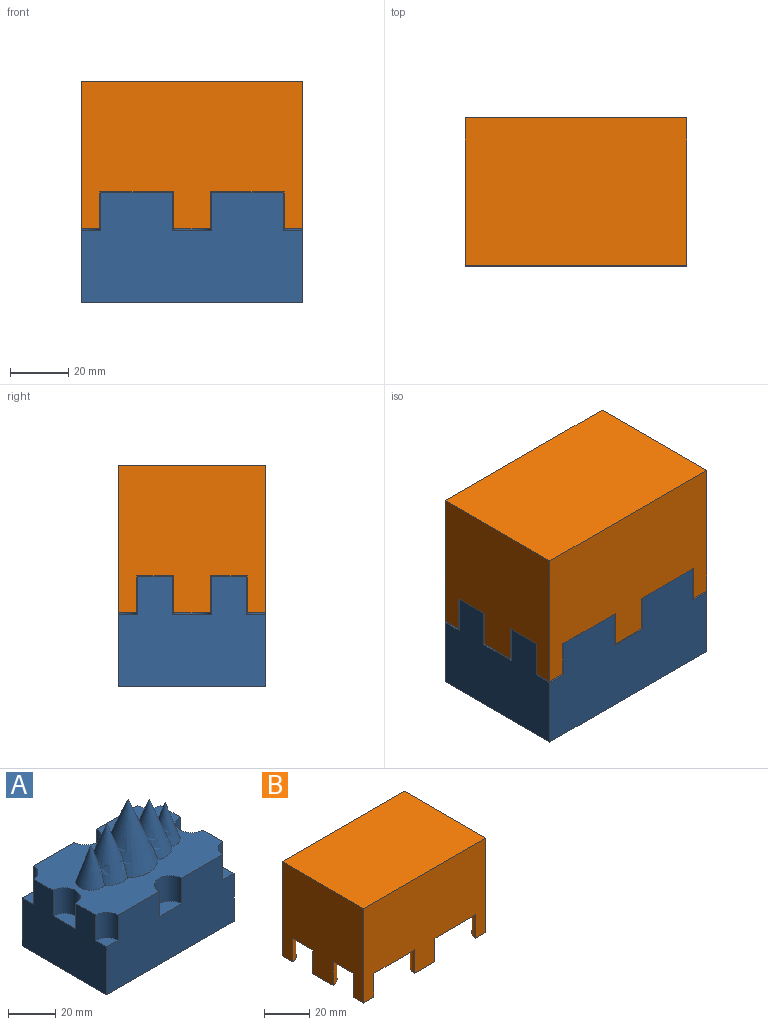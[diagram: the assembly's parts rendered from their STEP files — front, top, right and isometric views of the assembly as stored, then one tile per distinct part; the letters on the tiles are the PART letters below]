
ASSEMBLY  parts=2 mates=1
PART A: 27 faces, bbox 76.2x50.8x69.9 mm
  f0: plane 76.2x38.1mm, normal (0,-1,0), area 2547.6mm2, adj f1,f2,f4,f5,f17,f18,f21,f22
  f1: plane 50.8x38.1mm, normal (1,0,0), area 1579.9mm2, adj f0,f2,f3,f5,f15,f16,f23,f24
  f2: plane 76.22x50.82mm, normal (0,0,1), area 2461.3mm2, adj f0,f1,f3,f4,f6,f7,f8,f9
  f3: plane 76.2x38.1mm, normal (0,1,0), area 2547.6mm2, adj f1,f2,f4,f5,f13,f14,f19,f20
  f4: plane 50.8x38.1mm, normal (-1,0,0), area 1579.9mm2, adj f0,f2,f3,f5,f11,f12,f19,f20
  f5: plane 76.2x50.8mm, normal (0,0,-1), area 3871mm2, adj f0,f1,f3,f4
  f6: cone r=12.7mm half-angle=21.8deg, axis (0,0,-1), area 1139.2mm2, adj f2,f7,f9
  f7: cone r=9.53mm half-angle=20.6deg, axis (0,0,-1), area 632.6mm2, adj f2,f6,f8
  f8: cone r=6.35mm half-angle=18.4deg, axis (0,0,-1), area 338.3mm2, adj f2,f7
  f9: cone r=9.53mm half-angle=20.6deg, axis (0,0,-1), area 632.6mm2, adj f2,f6,f10
  f10: cone r=6.35mm half-angle=18.4deg, axis (0,0,-1), area 338.3mm2, adj f2,f9
  f11: cylinder r=6.73mm len=13.46mm, axis (0,0,1), area 279.3mm2, adj f2,f4,f12
  f12: plane 13.46x6.73mm, normal (0,0,1), area 71.2mm2, adj f4,f11
  f13: cylinder r=6.73mm len=13.46mm, axis (0,0,1), area 279.3mm2, adj f2,f3,f14
  f14: plane 13.46x6.73mm, normal (0,0,1), area 71.2mm2, adj f3,f13
  f15: cylinder r=6.73mm len=13.46mm, axis (0,0,1), area 279.3mm2, adj f1,f2,f16
  f16: plane 13.46x6.73mm, normal (0,0,1), area 71.2mm2, adj f1,f15
  f17: cylinder r=6.73mm len=13.46mm, axis (0,0,1), area 279.3mm2, adj f0,f2,f18
  f18: plane 13.46x6.73mm, normal (0,0,1), area 71.2mm2, adj f0,f17
  f19: cylinder r=6.73mm len=13.21mm, axis (0,0,1), area 139.6mm2, adj f2,f3,f4,f20
  f20: plane 6.73x6.73mm, normal (0,0,1), area 35.6mm2, adj f3,f4,f19
  f21: cylinder r=6.73mm len=13.21mm, axis (0,0,1), area 139.6mm2, adj f0,f2,f4,f22
  f22: plane 6.73x6.73mm, normal (0,0,1), area 35.6mm2, adj f0,f4,f21
  f23: cylinder r=6.73mm len=13.21mm, axis (0,0,1), area 139.6mm2, adj f1,f2,f3,f24
  f24: plane 6.73x6.73mm, normal (0,0,1), area 35.6mm2, adj f1,f3,f23
  f25: cylinder r=6.73mm len=13.21mm, axis (0,0,1), area 139.6mm2, adj f0,f1,f2,f26
  f26: plane 6.73x6.73mm, normal (0,0,1), area 35.6mm2, adj f0,f1,f25
PART B: 27 faces, bbox 76.2x50.8x50.8 mm
  f0: plane 76.21x50.81mm, normal (0,0,-1), area 2455.4mm2, adj f1,f2,f3,f4,f6,f8,f10,f12
  f1: plane 76.2x50.8mm, normal (0,1,0), area 3225.8mm2, adj f0,f2,f4,f5,f14,f15,f16,f17
  f2: plane 50.8x50.8mm, normal (-1,0,0), area 2258.1mm2, adj f0,f1,f3,f5,f6,f7,f18,f19
  f3: plane 76.2x50.8mm, normal (0,-1,0), area 3225.8mm2, adj f0,f2,f4,f5,f6,f7,f8,f9
  f4: plane 50.8x50.8mm, normal (1,0,0), area 2258.1mm2, adj f0,f1,f3,f5,f10,f11,f12,f13
  f5: plane 76.2x50.8mm, normal (0,0,1), area 3871mm2, adj f1,f2,f3,f4
  f6: cylinder r=6.35mm len=12.7mm, axis (0,0,1), area 126.7mm2, adj f0,f2,f3,f7
  f7: plane 6.35x6.35mm, normal (0,0,-1), area 31.7mm2, adj f2,f3,f6
  f8: cylinder r=6.35mm len=12.7mm, axis (0,0,1), area 253.4mm2, adj f0,f3,f9
  f9: plane 12.7x6.35mm, normal (0,0,-1), area 63.3mm2, adj f3,f8
  f10: cylinder r=6.35mm len=12.7mm, axis (0,0,1), area 126.7mm2, adj f0,f3,f4,f11
  f11: plane 6.35x6.35mm, normal (0,0,-1), area 31.7mm2, adj f3,f4,f10
  f12: cylinder r=6.35mm len=12.7mm, axis (0,0,1), area 253.4mm2, adj f0,f4,f13
  f13: plane 12.7x6.35mm, normal (0,0,-1), area 63.3mm2, adj f4,f12
  f14: cylinder r=6.35mm len=12.7mm, axis (0,0,1), area 126.7mm2, adj f0,f1,f4,f15
  f15: plane 6.35x6.35mm, normal (0,0,-1), area 31.7mm2, adj f1,f4,f14
  f16: cylinder r=6.35mm len=12.7mm, axis (0,0,1), area 253.4mm2, adj f0,f1,f17
  f17: plane 12.7x6.35mm, normal (0,0,-1), area 63.3mm2, adj f1,f16
  f18: cylinder r=6.35mm len=12.7mm, axis (0,0,1), area 126.7mm2, adj f0,f1,f2,f19
  f19: plane 6.35x6.35mm, normal (0,0,-1), area 31.7mm2, adj f1,f2,f18
  f20: cylinder r=6.35mm len=12.7mm, axis (0,0,1), area 253.4mm2, adj f0,f2,f21
  f21: plane 12.7x6.35mm, normal (0,0,-1), area 63.3mm2, adj f2,f20
  f22: cone r=13.08mm half-angle=21.9deg, axis (0,0,-1), area 1186.9mm2, adj f0,f23,f24
  f23: cone r=9.91mm half-angle=20.7deg, axis (0,0,-1), area 665.1mm2, adj f0,f22,f25
  f24: cone r=9.91mm half-angle=20.7deg, axis (0,0,-1), area 665.1mm2, adj f0,f22,f26
  f25: cone r=6.73mm half-angle=18.8deg, axis (0,0,-1), area 367.9mm2, adj f0,f23
  f26: cone r=6.73mm half-angle=18.8deg, axis (0,0,-1), area 367.9mm2, adj f0,f24
PLACE A t=(-58.8,8.63,-45.12)mm
PLACE B rot(axis=(0,0,1),0deg) t=(-58.8,8.63,-121.32)mm
MATE slider B.f22 <-> A.f6  axis (0,0,-1) through (-58.8,8.63,-45.12)mm
